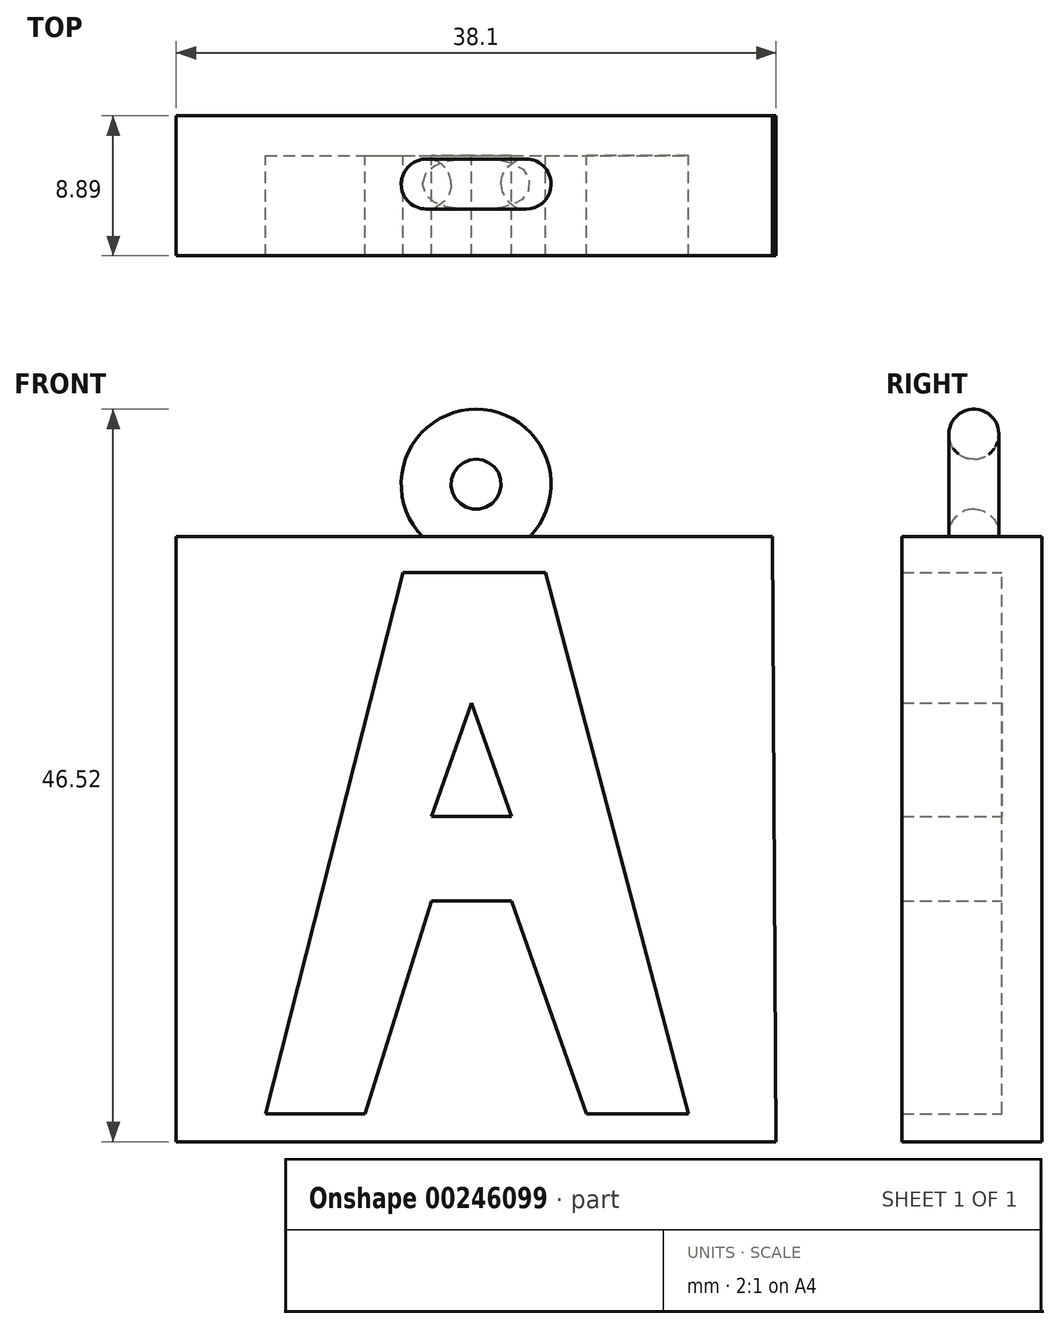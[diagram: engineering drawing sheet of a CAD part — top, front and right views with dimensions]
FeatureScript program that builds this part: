
annotation { "Feature Type Name" : "Feature", "Feature Type Description" : "" }
export const myFeature = defineFeature(function(context is Context, id is Id, definition is map)
    precondition{}
    {
        {
            var Q0;
            Q0=qCreatedBy(makeId("Front.planeOp"),FACE);
            var sketch = newSketch(context, id + "F0", { "sketchPlane" : qUnion([Q0])});
            skPoint(sketch, "E0.end.orphan", {"position": v(8.58, 21.22) * mm});
            skPoint(sketch, "E1.end.orphan", {"position": v(8.58, 32.54) * mm});
            skPoint(sketch, "E2.end.orphan", {"position": v(8.58, 13.5) * mm});
            skPoint(sketch, "E3.end.orphan", {"position": v(5.08, 0) * mm});
            skPoint(sketch, "E3.start.orphan", {"position": v(1.3, 0) * mm});
            skPoint(sketch, "E4.start.orphan", {"position": v(11.43, 0) * mm});
            skPoint(sketch, "E5.start.orphan", {"position": v(16.49, 0) * mm});
            skPoint(sketch, "E6.end.orphan", {"position": v(20.54, 0) * mm});
            skPoint(sketch, "E7.start.orphan", {"position": v(16.21, 32.54) * mm});
            skLineSegment(sketch, "E8", {"start": v(5.08, 0) * mm, "end": v(11.43, 0) * mm});
            skLineSegment(sketch, "E9", {"start": v(11.43, 0) * mm, "end": v(16.21, 15.28) * mm});
            skLineSegment(sketch, "E10", {"start": v(16.21, 15.28) * mm, "end": v(21.3, 15.28) * mm});
            skLineSegment(sketch, "E11", {"start": v(21.3, 15.28) * mm, "end": v(26.67, 0) * mm});
            skLineSegment(sketch, "E12", {"start": v(26.67, 0) * mm, "end": v(33.02, 0) * mm});
            skLineSegment(sketch, "E13", {"start": v(16.21, 20.67) * mm, "end": v(21.3, 20.67) * mm});
            skLineSegment(sketch, "E14", {"start": v(21.3, 20.67) * mm, "end": v(18.75, 27.85) * mm});
            skLineSegment(sketch, "E15", {"start": v(18.75, 27.85) * mm, "end": v(16.21, 20.67) * mm});
            skLineSegment(sketch, "E16", {"start": v(0, 0) * mm, "end": v(5.08, 0) * mm});
            skLineSegment(sketch, "E17", {"start": v(33.02, 0) * mm, "end": v(38.1, 0) * mm});
            skLineSegment(sketch, "E18", {"start": v(11.43, 0) * mm, "end": v(26.67, 0) * mm});
            skLineSegment(sketch, "E19", {"start": v(0, 38.43) * mm, "end": v(12.75, 38.43) * mm});
            skLineSegment(sketch, "E20", {"start": v(25.43, 38.44) * mm, "end": v(37.86, 38.45) * mm});
            skPoint(sketch, "E21.end.orphan", {"position": v(17.38, 37.8) * mm});
            skLineSegment(sketch, "E22", {"start": v(5.21, 0) * mm, "end": v(5.08, -0.67) * mm});
            skPoint(sketch, "E23.orphan", {"position": v(5.08, 30.79) * mm});
            skLineSegment(sketch, "E24", {"start": v(22.87, 38.44) * mm, "end": v(25.43, 38.44) * mm});
            skLineSegment(sketch, "E25", {"start": v(5.21, 0) * mm, "end": v(15, 38.43) * mm});
            skLineSegment(sketch, "E26", {"start": v(22.87, 38.44) * mm, "end": v(33.02, 0) * mm});
            skPoint(sketch, "E27.orphan", {"position": v(17.38, 38.44) * mm});
            skLineSegment(sketch, "E28", {"start": v(12.75, 38.43) * mm, "end": v(22.87, 38.44) * mm});
            skLineSegment(sketch, "E29", {"start": v(0, 38.43) * mm, "end": v(0, 0) * mm});
            skLineSegment(sketch, "E30", {"start": v(38.1, 0) * mm, "end": v(37.86, 38.45) * mm});
            skLineSegment(sketch, "E31", {"start": v(5.66, 1.78) * mm, "end": v(11.99, 1.78) * mm});
            skLineSegment(sketch, "E32", {"start": v(32.55, 1.78) * mm, "end": v(26.04, 1.78) * mm});
            skLineSegment(sketch, "E33", {"start": v(14.42, 36.15) * mm, "end": v(23.47, 36.15) * mm});
            skSolve(sketch);
        }
        {
            var Q0;
            Q0 = qSketchRegion(id + "F0", true);
            var Q1;
            Q1=makeQuery(id+"F0.imprint","IMPRINT",FACE,{"disambiguationData":[TD([[makeQuery(id+"F0.imprint","IMPRINT",EDGE,{"derivedFrom":sQuery(id+"F0.wireOp",EDGE,"E13")}),1.0]])]});
            var Q2;
            {var subQ2=sQuery(id+"F0.wireOp",EDGE,"E10");Q2=makeQuery(id+"F0.imprint","IMPRINT",FACE,{"disambiguationData":[TD([[makeQuery(id+"F0.imprint","IMPRINT",EDGE,{"derivedFrom":subQ2}),1.0]])]});}
            extrude(context, id + "F1", {"entities" : qUnion([Q0, Q1, Q2]), "oppositeDirection" : true, "depth" : 2.54 * mm});
        }
        {
            var Q0;
            {var subQ5=sQuery(id+"F0.wireOp",EDGE,"E16");Q0=makeQuery(id+"F0.imprint","IMPRINT",FACE,{"disambiguationData":[TD([[makeQuery(id+"F0.imprint","IMPRINT",EDGE,{"derivedFrom":subQ5}),1.0]])]});}
            var Q1;
            Q1=makeQuery(id+"F0.imprint","IMPRINT",FACE,{"disambiguationData":[TD([[makeQuery(id+"F0.imprint","IMPRINT",EDGE,{"derivedFrom":sQuery(id+"F0.wireOp",EDGE,"E13")}),1.0]])]});
            var Q2;
            {var subQ3=sQuery(id+"F0.wireOp",EDGE,"E17");Q2=makeQuery(id+"F0.imprint","IMPRINT",FACE,{"disambiguationData":[TD([[makeQuery(id+"F0.imprint","IMPRINT",EDGE,{"derivedFrom":subQ3}),1.0]])]});}
            var Q3;
            {var subQ1=sQuery(id+"F0.wireOp",EDGE,"E10");Q3=makeQuery(id+"F0.imprint","IMPRINT",FACE,{"disambiguationData":[TD([[makeQuery(id+"F0.imprint","IMPRINT",EDGE,{"derivedFrom":subQ1}),-1.0]])]});}
            var Q4;
            {var subQ3=sQuery(id+"F0.wireOp",EDGE,"E33");Q4=makeQuery(id+"F0.imprint","IMPRINT",FACE,{"disambiguationData":[TD([[makeQuery(id+"F0.imprint","IMPRINT",EDGE,{"derivedFrom":subQ3}),1.0]])]});}
            var Q5;
            {var subQ0=sQuery(id+"F0.wireOp",EDGE,"E12");Q5=makeQuery(id+"F0.imprint","IMPRINT",FACE,{"disambiguationData":[TD([[makeQuery(id+"F0.imprint","IMPRINT",EDGE,{"derivedFrom":subQ0}),1.0]])]});}
            var Q6;
            {var subQ5=sQuery(id+"F0.wireOp",EDGE,"E31");Q6=makeQuery(id+"F0.imprint","IMPRINT",FACE,{"disambiguationData":[TD([[makeQuery(id+"F0.imprint","IMPRINT",EDGE,{"derivedFrom":subQ5}),-1.0]])]});}
            extrude(context, id + "F2", {"entities" : qUnion([Q0, Q1, Q2, Q3, Q4, Q5, Q6]), "operationType" : NewBodyOperationType.ADD, "depth" : 6.35 * mm});
        }
        {
            var Q0;
            Q0=qCreatedBy(makeId("Right.planeOp"),FACE);
            cPlane(context, id + "F3", {"entities" : qUnion([Q0]), "cplaneType" : CPlaneType.OFFSET, "offset" : 19.05 * mm, "width" : 152.4 * mm, "height" : 152.4 * mm});
        }
        {
            var Q0;
            Q0=qCreatedBy(id+"F3.planeOp",FACE);
            var sketch = newSketch(context, id + "F4", { "sketchPlane" : qUnion([Q0])});
            skCircle(sketch, "E34", {"center": v(-1.8, 38.59) * mm, "radius": 1.59 * mm});
            skLineSegment(sketch, "E35", {"start": v(-1.8, 38.59) * mm, "end": v(-1.8, 41.76) * mm});
            skLineSegment(sketch, "E36", {"start": v(-1.8, 41.76) * mm, "end": v(5.69, 41.76) * mm});
            skSolve(sketch);
        }
        {
            var Q0;
            Q0 = qSketchRegion(id + "F4", true);
            var Q1;
            Q1=sQuery(id+"F4.wireOp",EDGE,"E36");
            revolve(context, id + "F5", {"operationType" : NewBodyOperationType.ADD, "entities" : qUnion([Q0]), "axis" : qUnion([Q1]), "revolveType" : RevolveType.FULL});
        }
    });
